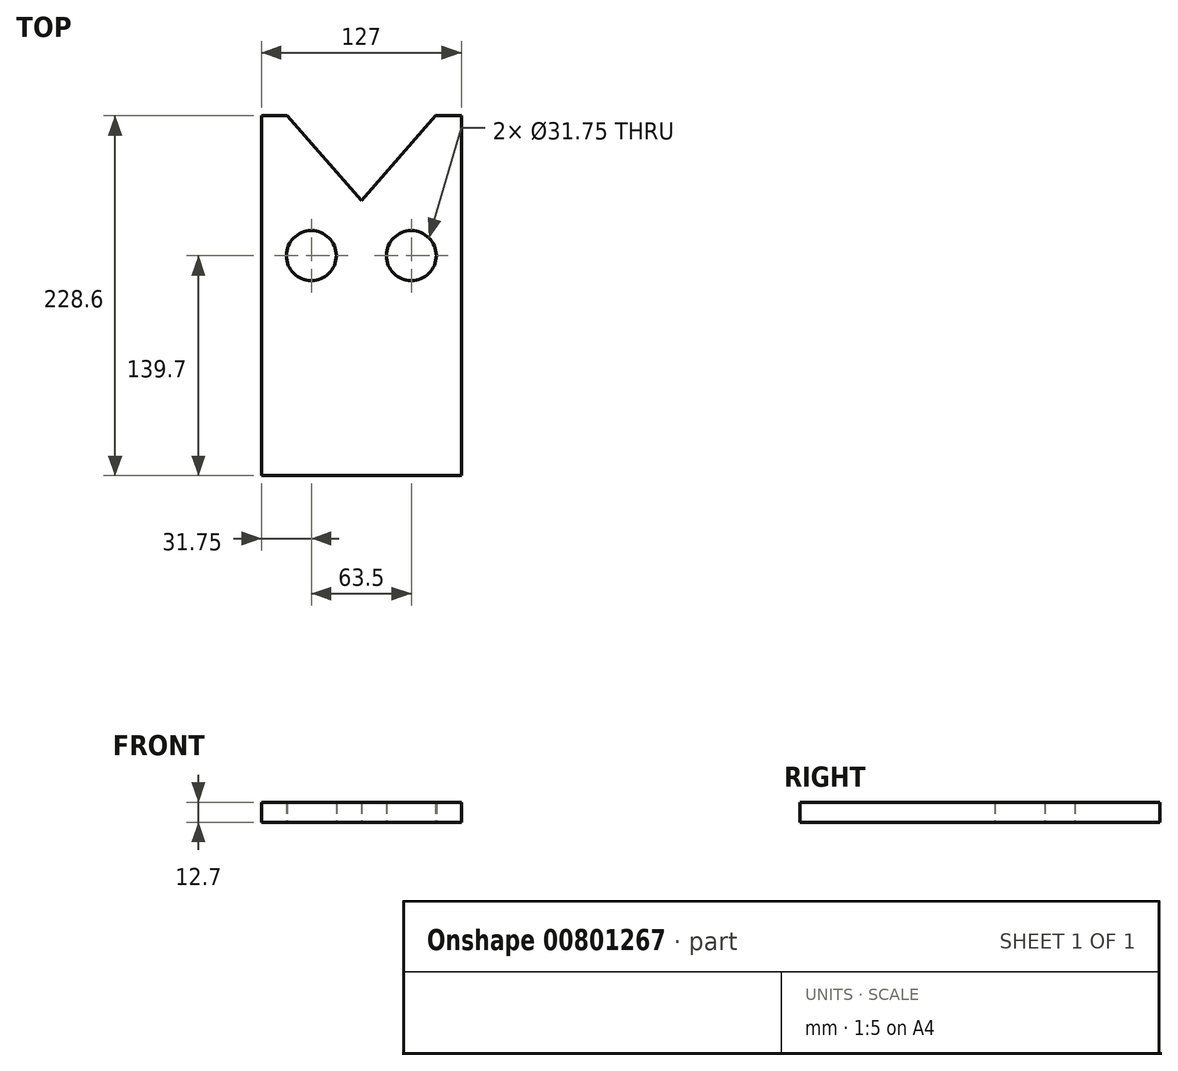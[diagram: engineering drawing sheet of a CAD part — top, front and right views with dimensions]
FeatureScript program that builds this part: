
annotation { "Feature Type Name" : "Feature", "Feature Type Description" : "" }
export const myFeature = defineFeature(function(context is Context, id is Id, definition is map)
    precondition{}
    {
        {
            var Q0;
            Q0=qCreatedBy(makeId("Top.planeOp"),FACE);
            var sketch = newSketch(context, id + "F0", { "sketchPlane" : qUnion([Q0])});
            skLineSegment(sketch, "E0.bottom", {"start": v(-63.5, -114.3) * mm, "end": v(63.5, -114.3) * mm});
            skLineSegment(sketch, "E0.top", {"start": v(-63.5, 114.3) * mm, "end": v(63.5, 114.3) * mm});
            skLineSegment(sketch, "E0.left", {"start": v(-63.5, -114.3) * mm, "end": v(-63.5, 114.3) * mm});
            skLineSegment(sketch, "E0.right", {"start": v(63.5, -114.3) * mm, "end": v(63.5, 114.3) * mm});
            skPoint(sketch, "E0.middle", {"position": v(0, 0) * mm});
            skCircle(sketch, "E1", {"center": v(-31.75, 25.4) * mm, "radius": 15.88 * mm});
            skCircle(sketch, "E2.MirrorC", {"center": v(31.75, 25.4) * mm, "radius": 15.88 * mm});
            skLineSegment(sketch, "E3", {"start": v(-47, 114.3) * mm, "end": v(0, 60.24) * mm});
            skLineSegment(sketch, "E4", {"start": v(0, 60.24) * mm, "end": v(47, 114.3) * mm});
            skLineSegment(sketch, "E5", {"start": v(47, 114.3) * mm, "end": v(-47, 114.3) * mm});
            skSolve(sketch);
        }
        {
            var Q0;
            Q0 = qSketchRegion(id + "F0", true);
            extrude(context, id + "F1", {"entities" : qUnion([Q0]), "depth" : 12.7 * mm, "offsetDistance" : 25.4 * mm});
        }
        {
            var Q0;
            Q0=makeQuery(id+"F0.imprint","IMPRINT",FACE,{"disambiguationData":[TD([[makeQuery(id+"F0.imprint","IMPRINT",EDGE,{"derivedFrom":sQuery(id+"F0.wireOp",EDGE,"E3")}),1.0]])]});
            extrude(context, id + "F2", {"entities" : qUnion([Q0]), "operationType" : NewBodyOperationType.REMOVE, "depth" : 25.4 * mm, "offsetDistance" : 25.4 * mm});
        }
    });
